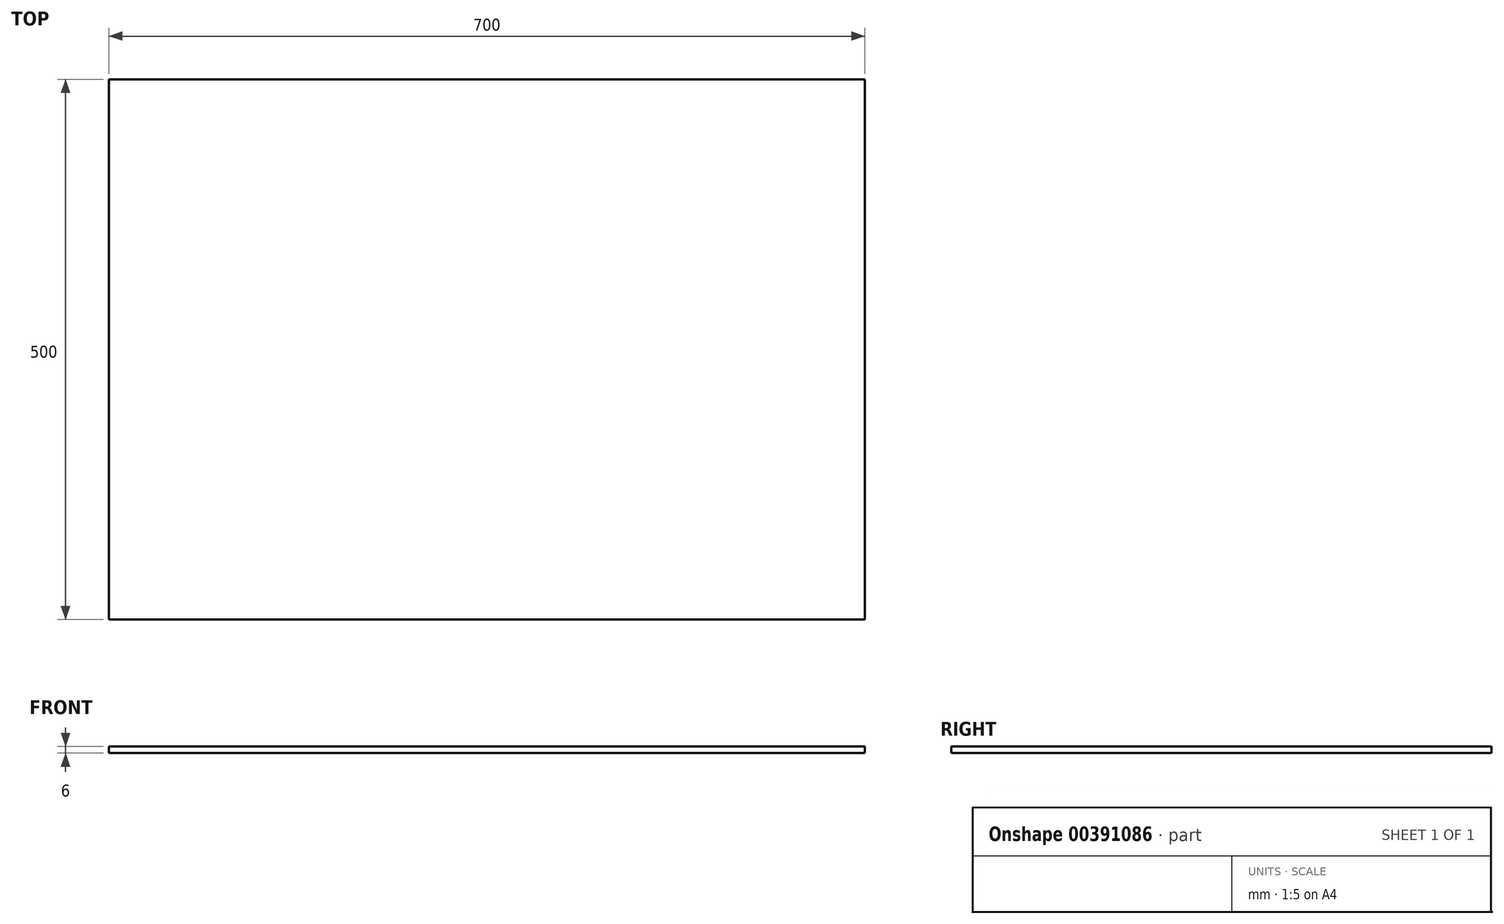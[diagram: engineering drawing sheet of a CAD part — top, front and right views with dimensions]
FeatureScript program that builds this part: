
annotation { "Feature Type Name" : "Feature", "Feature Type Description" : "" }
export const myFeature = defineFeature(function(context is Context, id is Id, definition is map)
    precondition{}
    {
        {
            var Q0;
            Q0=qCreatedBy(makeId("Top.planeOp"),FACE);
            var sketch = newSketch(context, id + "F0", { "sketchPlane" : qUnion([Q0])});
            skLineSegment(sketch, "E0.bottom", {"start": v(-350, 231.87) * mm, "end": v(350, 231.87) * mm});
            skLineSegment(sketch, "E0.top", {"start": v(-350, -268.13) * mm, "end": v(350, -268.13) * mm});
            skLineSegment(sketch, "E0.left", {"start": v(-350, 231.87) * mm, "end": v(-350, -268.13) * mm});
            skLineSegment(sketch, "E0.right", {"start": v(350, 231.87) * mm, "end": v(350, -268.13) * mm});
            skPoint(sketch, "E0.middle", {"position": v(0, -18.13) * mm});
            skSolve(sketch);
        }
        {
            var Q0;
            Q0=makeQuery(id+"F0.imprint","IMPRINT",FACE,{"disambiguationData":[TD([[makeQuery(id+"F0.imprint","IMPRINT",EDGE,{"derivedFrom":sQuery(id+"F0.wireOp",EDGE,"E0.bottom")}),-1.0]])]});
            extrude(context, id + "F1", {"entities" : qUnion([Q0]), "depth" : 6 * mm});
        }
    });
